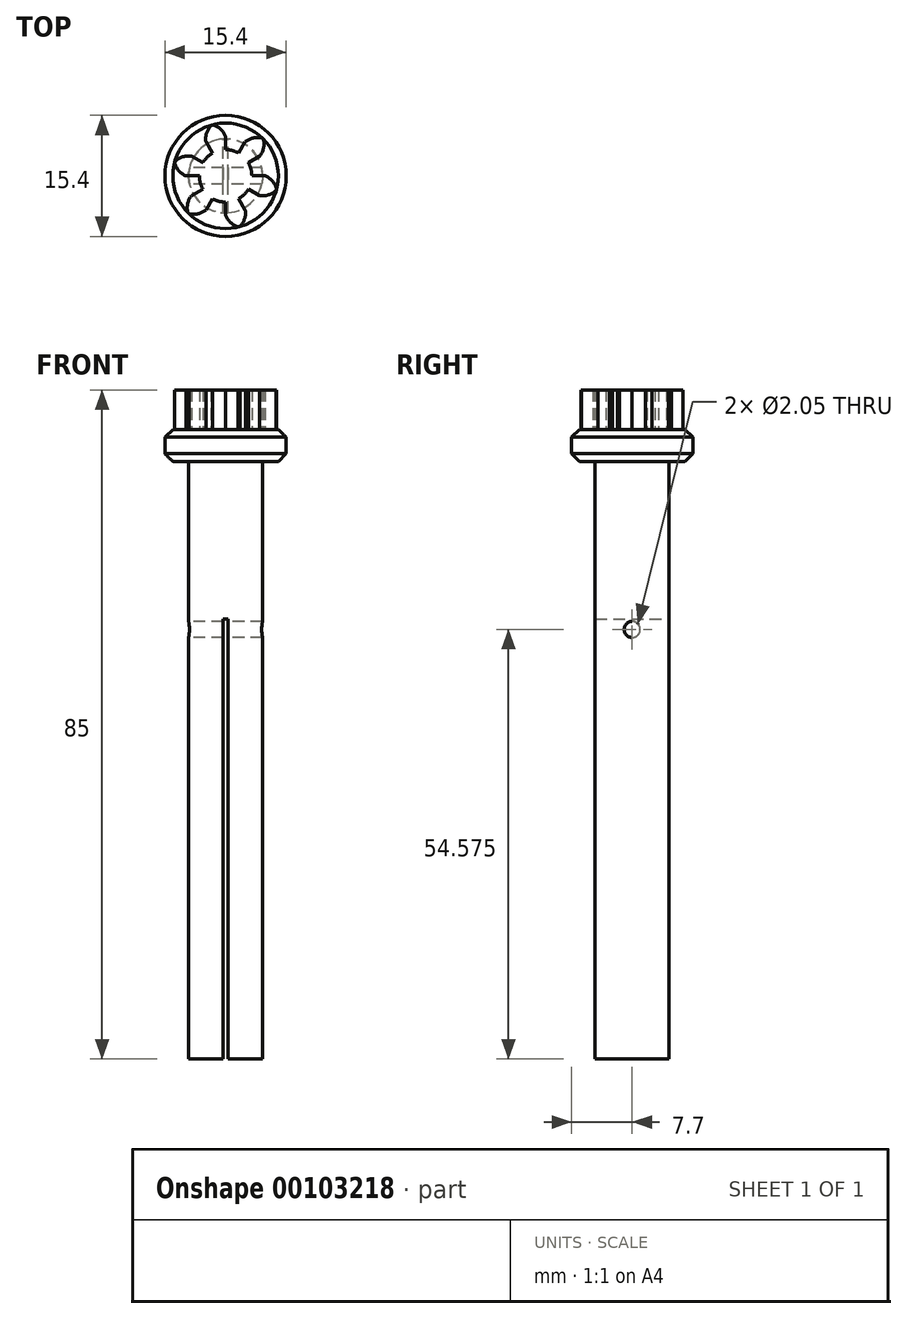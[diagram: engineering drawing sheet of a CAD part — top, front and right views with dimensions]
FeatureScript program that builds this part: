
annotation { "Feature Type Name" : "Feature", "Feature Type Description" : "" }
export const myFeature = defineFeature(function(context is Context, id is Id, definition is map)
    precondition{}
    {
        {
            assignVariable(context, id + "F0", {"name" : "PrintingOffset", "anyValue" : .3});
        }
        {
            assignVariable(context, id + "F1", {"name" : "ClampThickness", "anyValue" : 20});
        }
        {
            assignVariable(context, id + "F2", {"name" : "FilamentDiameter", "anyValue" : 1.75 + getVariable(context, 'PrintingOffset')});
        }
        {
            assignVariable(context, id + "F3", {"name" : "CollarThickness", "anyValue" : 2 * getVariable(context, 'FilamentDiameter')});
        }
        {
            assignVariable(context, id + "F4", {"name" : "ShaftLength", "anyValue" : 80});
        }
        {
            var Q0;
            Q0=qCreatedBy(makeId("Top.planeOp"),FACE);
            var sketch = newSketch(context, id + "F5", { "sketchPlane" : qUnion([Q0])});
            skCircle(sketch, "E0", {"center": v(0, 0) * mm, "radius": 5 * mm});
            skCircle(sketch, "E1", {"center": v(0, 0) * mm, "radius": 3.33 * mm});
            skCircle(sketch, "E2", {"center": v(0, 0) * mm, "radius": 6.67 * mm, "construction": true});
            skLineSegment(sketch, "E3", {"start": v(0, 0) * mm, "end": v(0, 7.61) * mm, "construction": true});
            skLineSegment(sketch, "E4", {"start": v(0, 0) * mm, "end": v(-4.4, 7.61) * mm, "construction": true});
            skLineSegment(sketch, "E5", {"start": v(-7.5, 5) * mm, "end": v(0, 5) * mm, "construction": true});
            skLineSegment(sketch, "E6", {"start": v(0, 5) * mm, "end": v(-7.5, 2.27) * mm, "construction": true});
            skLineSegment(sketch, "E7", {"start": v(0, 0) * mm, "end": v(-2.04, 7.61) * mm, "construction": true});
            skCircle(sketch, "E8", {"center": v(0, 5) * mm, "radius": 2.5 * mm, "construction": true});
            skCircle(sketch, "E9", {"center": v(0, 0) * mm, "radius": 4.7 * mm});
            skArc(sketch, "E10", {"start": v(0.1, 4.7) * mm, "mid": v(-0.52, 5.8) * mm, "end": v(-1.6, 6.47) * mm});
            skLineSegment(sketch, "E11", {"start": v(-1.6, 6.47) * mm, "end": v(-1.73, 6.44) * mm});
            skLineSegment(sketch, "E12", {"start": v(0, 5) * mm, "end": v(0, 3.33) * mm});
            skLineSegment(sketch, "E13.MirrorCS", {"start": v(-1.86, 6.4) * mm, "end": v(-1.73, 6.44) * mm});
            skArc(sketch, "E14.MirrorCS", {"start": v(-2.43, 4.02) * mm, "mid": v(-2.46, 5.29) * mm, "end": v(-1.86, 6.4) * mm});
            skLineSegment(sketch, "E15.MirrorCS", {"start": v(-2.5, 4.33) * mm, "end": v(-1.67, 2.89) * mm});
            skLineSegment(sketch, "E16.1.0", {"start": v(-4.33, 2.5) * mm, "end": v(-2.89, 1.67) * mm});
            skArc(sketch, "E16.1.1", {"start": v(-4.02, 2.43) * mm, "mid": v(-5.29, 2.46) * mm, "end": v(-6.4, 1.86) * mm});
            skArc(sketch, "E16.1.2", {"start": v(-4.7, -0.1) * mm, "mid": v(-5.8, 0.52) * mm, "end": v(-6.47, 1.6) * mm});
            skLineSegment(sketch, "E16.1.3", {"start": v(-6.47, 1.6) * mm, "end": v(-6.44, 1.73) * mm});
            skLineSegment(sketch, "E16.1.4", {"start": v(-6.4, 1.86) * mm, "end": v(-6.44, 1.73) * mm});
            skLineSegment(sketch, "E16.1.5", {"start": v(-5, 0) * mm, "end": v(-3.33, 0) * mm});
            skLineSegment(sketch, "E16.2.0", {"start": v(-4.33, -2.5) * mm, "end": v(-2.89, -1.67) * mm});
            skArc(sketch, "E16.2.1", {"start": v(-4.12, -2.26) * mm, "mid": v(-4.77, -3.35) * mm, "end": v(-4.8, -4.62) * mm});
            skArc(sketch, "E16.2.2", {"start": v(-2.26, -4.12) * mm, "mid": v(-3.35, -4.77) * mm, "end": v(-4.62, -4.8) * mm});
            skLineSegment(sketch, "E16.2.3", {"start": v(-4.62, -4.8) * mm, "end": v(-4.72, -4.72) * mm});
            skLineSegment(sketch, "E16.2.4", {"start": v(-4.8, -4.62) * mm, "end": v(-4.72, -4.72) * mm});
            skLineSegment(sketch, "E16.2.5", {"start": v(-2.5, -4.33) * mm, "end": v(-1.67, -2.89) * mm});
            skLineSegment(sketch, "E16.3.0", {"start": v(0, -5) * mm, "end": v(0, -3.33) * mm});
            skArc(sketch, "E16.3.1", {"start": v(-0.1, -4.7) * mm, "mid": v(0.52, -5.8) * mm, "end": v(1.6, -6.47) * mm});
            skArc(sketch, "E16.3.2", {"start": v(2.43, -4.02) * mm, "mid": v(2.46, -5.29) * mm, "end": v(1.86, -6.4) * mm});
            skLineSegment(sketch, "E16.3.3", {"start": v(1.86, -6.4) * mm, "end": v(1.73, -6.44) * mm});
            skLineSegment(sketch, "E16.3.4", {"start": v(1.6, -6.47) * mm, "end": v(1.73, -6.44) * mm});
            skLineSegment(sketch, "E16.3.5", {"start": v(2.5, -4.33) * mm, "end": v(1.67, -2.89) * mm});
            skLineSegment(sketch, "E16.4.0", {"start": v(4.33, -2.5) * mm, "end": v(2.89, -1.67) * mm});
            skArc(sketch, "E16.4.1", {"start": v(4.02, -2.43) * mm, "mid": v(5.29, -2.46) * mm, "end": v(6.4, -1.86) * mm});
            skArc(sketch, "E16.4.2", {"start": v(4.7, 0.1) * mm, "mid": v(5.8, -0.52) * mm, "end": v(6.47, -1.6) * mm});
            skLineSegment(sketch, "E16.4.3", {"start": v(6.47, -1.6) * mm, "end": v(6.44, -1.73) * mm});
            skLineSegment(sketch, "E16.4.4", {"start": v(6.4, -1.86) * mm, "end": v(6.44, -1.73) * mm});
            skLineSegment(sketch, "E16.4.5", {"start": v(5, 0) * mm, "end": v(3.33, 0) * mm});
            skLineSegment(sketch, "E16.5.0", {"start": v(4.33, 2.5) * mm, "end": v(2.89, 1.67) * mm});
            skArc(sketch, "E16.5.1", {"start": v(4.12, 2.26) * mm, "mid": v(4.77, 3.35) * mm, "end": v(4.8, 4.62) * mm});
            skArc(sketch, "E16.5.2", {"start": v(2.26, 4.12) * mm, "mid": v(3.35, 4.77) * mm, "end": v(4.62, 4.8) * mm});
            skLineSegment(sketch, "E16.5.3", {"start": v(4.62, 4.8) * mm, "end": v(4.72, 4.72) * mm});
            skLineSegment(sketch, "E16.5.4", {"start": v(4.8, 4.62) * mm, "end": v(4.72, 4.72) * mm});
            skLineSegment(sketch, "E16.5.5", {"start": v(2.5, 4.33) * mm, "end": v(1.67, 2.89) * mm});
            skSolve(sketch);
        }
        {
            var Q0;
            {var subQ0=sQuery(id+"F5.wireOp",EDGE,"E16.1.0");Q0=makeQuery(id+"F5.imprint","IMPRINT",FACE,{"disambiguationData":[TD([[makeQuery(id+"F5.imprint","IMPRINT",EDGE,{"derivedFrom":subQ0}),-1.0]])]});}
            var Q1;
            {var subQ1=sQuery(id+"F5.wireOp",EDGE,"E11");Q1=makeQuery(id+"F5.imprint","IMPRINT",FACE,{"disambiguationData":[TD([[makeQuery(id+"F5.imprint","IMPRINT",EDGE,{"derivedFrom":subQ1}),1.0]])]});}
            var Q2;
            {var subQ0=sQuery(id+"F5.wireOp",EDGE,"E1");var subQ3=makeQuery(id+"F5.imprint","INTERSECT",VERTEX,{"derivedFrom":[subQ0,sQuery(id+"F5.wireOp",EDGE,"E16.4.5")]});Q2=makeQuery(id+"F5.imprint","IMPRINT",FACE,{"disambiguationData":[TD([[makeQuery(id+"F5.imprint","IMPRINT",EDGE,{"disambiguationData":[TD([[subQ3,-1.0]])],"derivedFrom":subQ0}),1.0]])]});}
            var Q3;
            {var subQ4=sQuery(id+"F5.wireOp",EDGE,"E16.5.0");Q3=makeQuery(id+"F5.imprint","IMPRINT",FACE,{"disambiguationData":[TD([[makeQuery(id+"F5.imprint","IMPRINT",EDGE,{"derivedFrom":subQ4}),-1.0]])]});}
            var Q4;
            {var subQ4=sQuery(id+"F5.wireOp",EDGE,"E16.4.0");Q4=makeQuery(id+"F5.imprint","IMPRINT",FACE,{"disambiguationData":[TD([[makeQuery(id+"F5.imprint","IMPRINT",EDGE,{"derivedFrom":subQ4}),-1.0]])]});}
            var Q5;
            {var subQ4=sQuery(id+"F5.wireOp",EDGE,"E16.3.0");Q5=makeQuery(id+"F5.imprint","IMPRINT",FACE,{"disambiguationData":[TD([[makeQuery(id+"F5.imprint","IMPRINT",EDGE,{"derivedFrom":subQ4}),-1.0]])]});}
            var Q6;
            {var subQ4=sQuery(id+"F5.wireOp",EDGE,"E16.2.0");Q6=makeQuery(id+"F5.imprint","IMPRINT",FACE,{"disambiguationData":[TD([[makeQuery(id+"F5.imprint","IMPRINT",EDGE,{"derivedFrom":subQ4}),-1.0]])]});}
            var Q7;
            {var subQ0=sQuery(id+"F5.wireOp",EDGE,"E12");Q7=makeQuery(id+"F5.imprint","IMPRINT",FACE,{"disambiguationData":[TD([[makeQuery(id+"F5.imprint","IMPRINT",EDGE,{"derivedFrom":subQ0}),-1.0]])]});}
            var Q8;
            {var subQ0=sQuery(id+"F5.wireOp",EDGE,"E16.1.3");Q8=makeQuery(id+"F5.imprint","IMPRINT",FACE,{"disambiguationData":[TD([[makeQuery(id+"F5.imprint","IMPRINT",EDGE,{"derivedFrom":subQ0}),-1.0]])]});}
            var Q9;
            {var subQ0=sQuery(id+"F5.wireOp",EDGE,"E16.2.3");Q9=makeQuery(id+"F5.imprint","IMPRINT",FACE,{"disambiguationData":[TD([[makeQuery(id+"F5.imprint","IMPRINT",EDGE,{"derivedFrom":subQ0}),-1.0]])]});}
            var Q10;
            {var subQ0=sQuery(id+"F5.wireOp",EDGE,"E16.3.3");Q10=makeQuery(id+"F5.imprint","IMPRINT",FACE,{"disambiguationData":[TD([[makeQuery(id+"F5.imprint","IMPRINT",EDGE,{"derivedFrom":subQ0}),-1.0]])]});}
            var Q11;
            {var subQ0=sQuery(id+"F5.wireOp",EDGE,"E16.4.3");Q11=makeQuery(id+"F5.imprint","IMPRINT",FACE,{"disambiguationData":[TD([[makeQuery(id+"F5.imprint","IMPRINT",EDGE,{"derivedFrom":subQ0}),-1.0]])]});}
            var Q12;
            {var subQ0=sQuery(id+"F5.wireOp",EDGE,"E16.5.3");Q12=makeQuery(id+"F5.imprint","IMPRINT",FACE,{"disambiguationData":[TD([[makeQuery(id+"F5.imprint","IMPRINT",EDGE,{"derivedFrom":subQ0}),-1.0]])]});}
            extrude(context, id + "F6", {"entities" : qUnion([Q0, Q1, Q2, Q3, Q4, Q5, Q6, Q7, Q8, Q9, Q10, Q11, Q12]), "depth" : 5 * mm});
        }
        {
            var Q0;
            {var subQ0=sQuery(id+"F5.wireOp",EDGE,"E1");var subQ8=makeQuery(id+"F5.imprint","INTERSECT",VERTEX,{"derivedFrom":[subQ0,sQuery(id+"F5.wireOp",EDGE,"E16.4.5")]});Q0=makeQuery(id+"F5.imprint","IMPRINT",FACE,{"disambiguationData":[TD([[makeQuery(id+"F5.imprint","IMPRINT",EDGE,{"disambiguationData":[TD([[subQ8,-1.0]])],"derivedFrom":subQ0}),1.0]])]});}
            var Q1;
            {var subQ5=sQuery(id+"F5.wireOp",EDGE,"E1");var subQ7=sQuery(id+"F5.wireOp",EDGE,"E16.1.5");var subQ9=makeQuery(id+"F5.imprint","INTERSECT",VERTEX,{"derivedFrom":[subQ5,subQ7]});Q1=makeQuery(id+"F5.imprint","IMPRINT",FACE,{"disambiguationData":[TD([[makeQuery(id+"F5.imprint","IMPRINT",EDGE,{"disambiguationData":[TD([[subQ9,-1.0]])],"derivedFrom":subQ5}),-1.0]])]});}
            var Q2;
            {var subQ0=sQuery(id+"F5.wireOp",EDGE,"E16.1.0");var subQ1=sQuery(id+"F5.wireOp",EDGE,"E1");var subQ2=makeQuery(id+"F5.imprint","INTERSECT",VERTEX,{"derivedFrom":[subQ1,subQ0]});Q2=makeQuery(id+"F5.imprint","IMPRINT",FACE,{"disambiguationData":[TD([[makeQuery(id+"F5.imprint","IMPRINT",EDGE,{"disambiguationData":[TD([[subQ2,-1.0]])],"derivedFrom":subQ1}),-1.0]])]});}
            var Q3;
            {var subQ5=sQuery(id+"F5.wireOp",EDGE,"E15.MirrorCS");var subQ7=sQuery(id+"F5.wireOp",EDGE,"E1");var subQ9=makeQuery(id+"F5.imprint","INTERSECT",VERTEX,{"derivedFrom":[subQ7,subQ5]});Q3=makeQuery(id+"F5.imprint","IMPRINT",FACE,{"disambiguationData":[TD([[makeQuery(id+"F5.imprint","IMPRINT",EDGE,{"disambiguationData":[TD([[subQ9,-1.0]])],"derivedFrom":subQ7}),-1.0]])]});}
            var Q4;
            {var subQ0=sQuery(id+"F5.wireOp",EDGE,"E12");var subQ1=sQuery(id+"F5.wireOp",EDGE,"E1");var subQ2=makeQuery(id+"F5.imprint","INTERSECT",VERTEX,{"derivedFrom":[subQ1,subQ0]});Q4=makeQuery(id+"F5.imprint","IMPRINT",FACE,{"disambiguationData":[TD([[makeQuery(id+"F5.imprint","IMPRINT",EDGE,{"disambiguationData":[TD([[subQ2,-1.0]])],"derivedFrom":subQ1}),-1.0]])]});}
            var Q5;
            {var subQ2=sQuery(id+"F5.wireOp",EDGE,"E12");var subQ7=sQuery(id+"F5.wireOp",EDGE,"E1");var subQ8=makeQuery(id+"F5.imprint","INTERSECT",VERTEX,{"derivedFrom":[subQ7,subQ2]});Q5=makeQuery(id+"F5.imprint","IMPRINT",FACE,{"disambiguationData":[TD([[makeQuery(id+"F5.imprint","IMPRINT",EDGE,{"disambiguationData":[TD([[subQ8,1.0]])],"derivedFrom":subQ7}),-1.0]])]});}
            var Q6;
            {var subQ0=sQuery(id+"F5.wireOp",EDGE,"E16.5.0");var subQ1=sQuery(id+"F5.wireOp",EDGE,"E1");var subQ2=makeQuery(id+"F5.imprint","INTERSECT",VERTEX,{"derivedFrom":[subQ1,subQ0]});Q6=makeQuery(id+"F5.imprint","IMPRINT",FACE,{"disambiguationData":[TD([[makeQuery(id+"F5.imprint","IMPRINT",EDGE,{"disambiguationData":[TD([[subQ2,-1.0]])],"derivedFrom":subQ1}),-1.0]])]});}
            var Q7;
            {var subQ5=sQuery(id+"F5.wireOp",EDGE,"E16.4.5");var subQ7=sQuery(id+"F5.wireOp",EDGE,"E1");var subQ8=makeQuery(id+"F5.imprint","INTERSECT",VERTEX,{"derivedFrom":[subQ7,subQ5]});Q7=makeQuery(id+"F5.imprint","IMPRINT",FACE,{"disambiguationData":[TD([[makeQuery(id+"F5.imprint","IMPRINT",EDGE,{"disambiguationData":[TD([[subQ8,-1.0]])],"derivedFrom":subQ7}),-1.0]])]});}
            var Q8;
            {var subQ0=sQuery(id+"F5.wireOp",EDGE,"E16.4.0");var subQ1=sQuery(id+"F5.wireOp",EDGE,"E1");var subQ2=makeQuery(id+"F5.imprint","INTERSECT",VERTEX,{"derivedFrom":[subQ1,subQ0]});Q8=makeQuery(id+"F5.imprint","IMPRINT",FACE,{"disambiguationData":[TD([[makeQuery(id+"F5.imprint","IMPRINT",EDGE,{"disambiguationData":[TD([[subQ2,-1.0]])],"derivedFrom":subQ1}),-1.0]])]});}
            var Q9;
            {var subQ5=sQuery(id+"F5.wireOp",EDGE,"E16.3.5");var subQ7=sQuery(id+"F5.wireOp",EDGE,"E1");var subQ8=makeQuery(id+"F5.imprint","INTERSECT",VERTEX,{"derivedFrom":[subQ7,subQ5]});Q9=makeQuery(id+"F5.imprint","IMPRINT",FACE,{"disambiguationData":[TD([[makeQuery(id+"F5.imprint","IMPRINT",EDGE,{"disambiguationData":[TD([[subQ8,-1.0]])],"derivedFrom":subQ7}),-1.0]])]});}
            var Q10;
            {var subQ0=sQuery(id+"F5.wireOp",EDGE,"E16.3.0");var subQ1=sQuery(id+"F5.wireOp",EDGE,"E1");var subQ2=makeQuery(id+"F5.imprint","INTERSECT",VERTEX,{"derivedFrom":[subQ1,subQ0]});Q10=makeQuery(id+"F5.imprint","IMPRINT",FACE,{"disambiguationData":[TD([[makeQuery(id+"F5.imprint","IMPRINT",EDGE,{"disambiguationData":[TD([[subQ2,-1.0]])],"derivedFrom":subQ1}),-1.0]])]});}
            var Q11;
            {var subQ5=sQuery(id+"F5.wireOp",EDGE,"E1");var subQ7=sQuery(id+"F5.wireOp",EDGE,"E16.2.5");var subQ9=makeQuery(id+"F5.imprint","INTERSECT",VERTEX,{"derivedFrom":[subQ5,subQ7]});Q11=makeQuery(id+"F5.imprint","IMPRINT",FACE,{"disambiguationData":[TD([[makeQuery(id+"F5.imprint","IMPRINT",EDGE,{"disambiguationData":[TD([[subQ9,-1.0]])],"derivedFrom":subQ5}),-1.0]])]});}
            var Q12;
            {var subQ0=sQuery(id+"F5.wireOp",EDGE,"E16.2.0");var subQ1=sQuery(id+"F5.wireOp",EDGE,"E1");var subQ2=makeQuery(id+"F5.imprint","INTERSECT",VERTEX,{"derivedFrom":[subQ1,subQ0]});Q12=makeQuery(id+"F5.imprint","IMPRINT",FACE,{"disambiguationData":[TD([[makeQuery(id+"F5.imprint","IMPRINT",EDGE,{"disambiguationData":[TD([[subQ2,-1.0]])],"derivedFrom":subQ1}),-1.0]])]});}
            extrude(context, id + "F7", {"entities" : qUnion([Q0, Q1, Q2, Q3, Q4, Q5, Q6, Q7, Q8, Q9, Q10, Q11, Q12]), "operationType" : NewBodyOperationType.ADD, "oppositeDirection" : true, "depth" : (getVariable(context, 'ShaftLength')) * mm});
        }
        {
            var Q0;
            Q0=makeQuery(id+"F7.opExtrude","CAP_FACE",FACE,{"disambiguationData":[OSD([sQuery(id+"F5.wireOp",EDGE,"E9")])],"isStart":false});
            var sketch = newSketch(context, id + "F8", { "sketchPlane" : qUnion([Q0])});
            skLineSegment(sketch, "E17", {"start": v(0, 4.7) * mm, "end": v(0, -4.7) * mm, "construction": true});
            skLineSegment(sketch, "E18", {"start": v(-0.3, 4.69) * mm, "end": v(-0.3, -4.69) * mm});
            skLineSegment(sketch, "E19.MirrorCS", {"start": v(0.3, 4.69) * mm, "end": v(0.3, -4.69) * mm});
            skCircle(sketch, "E20.0", {"center": v(0, 0) * mm, "radius": 4.7 * mm});
            skCircle(sketch, "E21.0", {"center": v(0, 0) * mm, "radius": 7.7 * mm});
            skSolve(sketch);
        }
        {
            var Q0;
            Q0=makeQuery(id+"F8.imprint","IMPRINT",FACE,{"disambiguationData":[TD([[makeQuery(id+"F8.imprint","IMPRINT",EDGE,{"derivedFrom":sQuery(id+"F8.wireOp",EDGE,"E21.0")}),1.0]])]});
            extrude(context, id + "F9", {"entities" : qUnion([Q0]), "operationType" : NewBodyOperationType.ADD, "oppositeDirection" : true, "depth" : (getVariable(context, 'ShaftLength')) * mm, "hasSecondDirection" : true, "secondDirectionOppositeDirection" : true, "secondDirectionDepth" : (getVariable(context, 'ShaftLength') - getVariable(context, 'CollarThickness')) * mm});
        }
        {
            var Q0;
            Q0=makeQuery(id+"F9.opExtrude","CAP_EDGE",EDGE,{"disambiguationData":[OSD([sQuery(id+"F8.wireOp",EDGE,"39c6af55-2d96-489b-a5a8-3c761cad1f90.0")])],"isStart":false});
            var Q1;
            Q1=makeQuery(id+"F9.opExtrude","CAP_EDGE",EDGE,{"disambiguationData":[OSD([sQuery(id+"F8.wireOp",EDGE,"39c6af55-2d96-489b-a5a8-3c761cad1f90.0")])],"isStart":true});
            var Q2;
            Q2=makeQuery(id+"F9.opExtrude","CAP_EDGE",EDGE,{"disambiguationData":[OSD([sQuery(id+"F8.wireOp",EDGE,"E21.0")])],"isStart":false});
            var Q3;
            Q3=makeQuery(id+"F9.opExtrude","CAP_EDGE",EDGE,{"disambiguationData":[OSD([sQuery(id+"F8.wireOp",EDGE,"E21.0")])],"isStart":true});
            chamfer(context, id + "F10", {"entities" : qUnion([Q0, Q1, Q2, Q3]), "width" : 1 * mm, "tangentPropagation" : true});
        }
        {
            var Q0;
            {var subQ0=sQuery(id+"F8.wireOp",EDGE,"E18");Q0=makeQuery(id+"F8.imprint","IMPRINT",FACE,{"disambiguationData":[TD([[makeQuery(id+"F8.imprint","IMPRINT",EDGE,{"derivedFrom":subQ0}),1.0]])]});}
            extrude(context, id + "F11", {"entities" : qUnion([Q0]), "operationType" : NewBodyOperationType.REMOVE, "oppositeDirection" : true, "depth" : (getVariable(context, 'ShaftLength') - getVariable(context, 'ClampThickness') - getVariable(context, 'CollarThickness')) * mm});
        }
        {
            var Q0;
            Q0=qCreatedBy(makeId("Right.planeOp"),FACE);
            var sketch = newSketch(context, id + "F12", { "sketchPlane" : qUnion([Q0])});
            skLineSegment(sketch, "E22", {"start": v(0, -80) * mm, "end": v(0, 0) * mm, "construction": true});
            skPoint(sketch, "E23", {"position": v(0, -24.1) * mm});
            skCircle(sketch, "E24", {"center": v(0, -25.43) * mm, "radius": 1.02 * mm});
            skLineSegment(sketch, "E25.0", {"start": v(-4.69, -80) * mm, "end": v(4.69, -80) * mm});
            skSolve(sketch);
        }
        {
            var Q0;
            Q0=makeQuery(id+"F12.imprint","IMPRINT",FACE,{"disambiguationData":[TD([[makeQuery(id+"F12.imprint","IMPRINT",EDGE,{"derivedFrom":sQuery(id+"F12.wireOp",EDGE,"E24")}),1.0]])]});
            extrude(context, id + "F13", {"entities" : qUnion([Q0]), "operationType" : NewBodyOperationType.REMOVE, "endBound" : BoundingType.THROUGH_ALL, "depth" : 25 * mm, "hasSecondDirection" : true, "secondDirectionBound" : SecondDirectionBoundingType.THROUGH_ALL, "secondDirectionOppositeDirection" : true, "secondDirectionDepth" : 25 * mm});
        }
    });
